# Revit family: Circular diffuser-Extract
name_source: partatom
category: Air Terminals
revit_build: Autodesk Revit MEP 2013 (Build: 20130531_2115(x64)
units: mm (PartAtom-declared; Revit-internal decimal feet)

## types (8) — shared parameters
Manufacturer = Anemostat
Model = C-27
URL = http://www.anemostat.com

## per-type parameters (varying)
| type | A - Outer Cone Radius | A Outer Cone | C1 A | C1 B | C1 B Radius | C1 C | C1 C Radius | C2 & 3 A | C2 B | C2 B Radius | C2 C | C2 C Radius | C3 B | C3 B Radius | C3 C | C3 C Radius | Diffuser Service | Duct | Duct Radius | Outer Cone Height | R Neck Height | U - Outer Cone Radius | U Outer Cone | Z |
| C-27 06" | 276.2 mm | 552.5 mm | 57.9 mm | 102 mm | 51 mm | 34.9 mm | 17.5 mm | 54.8 mm | 217.5 mm | 108.7 mm | 108 mm | 54 mm | 385 mm | 192.5 mm | 209.6 mm | 104.8 mm | SCD | 300 mm | 150 mm | 70.6 mm | 76.2 mm  [stored 0.25 ft] | 308 mm | 616 mm | 25.4 mm  [stored 0.0833333 ft] |
| C-27 08" | 208 mm | 415.9 mm | 42.1 mm | 67.5 mm | 33.7 mm | 27 mm | 13.5 mm | 38.9 mm | 161.9 mm | 81 mm | 84.1 mm | 42.1 mm | 288.1 mm | 144.1 mm | 163.5 mm | 81.8 mm | SCD | 203.2 mm | 101.6 mm | 52.4 mm | 76.2 mm  [stored 0.25 ft] | 233.4 mm | 466.7 mm | 15.9 mm |
| C-27 10" | 276.2 mm | 552.5 mm | 57.9 mm | 102 mm | 51 mm | 34.9 mm | 17.5 mm | 54.8 mm | 217.5 mm | 108.7 mm | 108 mm | 54 mm | 385 mm | 192.5 mm | 209.6 mm | 104.8 mm | SCD | 250 mm | 125 mm | 79.4 mm | 76.2 mm  [stored 0.25 ft] | 308 mm | 616 mm | 25.4 mm  [stored 0.0833333 ft] |
| C-27 12" | 276.2 mm | 552.5 mm | 57.9 mm | 102 mm | 51 mm | 34.9 mm | 17.5 mm | 54.8 mm | 217.5 mm | 108.7 mm | 108 mm | 54 mm | 385 mm | 192.5 mm | 209.6 mm | 104.8 mm | ECD | 300 mm | 150 mm | 70.6 mm | 76.2 mm  [stored 0.25 ft] | 308 mm | 616 mm | 25.4 mm  [stored 0.0833333 ft] |
| C-27 15" | 403.2 mm | 806.5 mm | 76.2 mm  [stored 0.25 ft] | 141.3 mm | 70.6 mm | 38.1 mm  [stored 0.125 ft] | 19.1 mm | 85.7 mm | 311.2 mm | 155.6 mm | 139.7 mm | 69.9 mm | 558.8 mm | 279.4 mm | 284.2 mm | 142.1 mm | SCD | 381 mm | 190.5 mm | 99.2 mm | 76.2 mm  [stored 0.25 ft] | 450.9 mm | 901.7 mm | 34.9 mm |
| C-27 18" | 403.2 mm | 806.5 mm | 76.2 mm  [stored 0.25 ft] | 141.3 mm | 70.6 mm | 38.1 mm  [stored 0.125 ft] | 19.1 mm | 85.7 mm | 311.2 mm | 155.6 mm | 139.7 mm | 69.9 mm | 558.8 mm | 279.4 mm | 284.2 mm | 142.1 mm | SCD | 457.2 mm | 228.6 mm | 76.2 mm  [stored 0.25 ft] | 82.6 mm | 450.9 mm | 901.7 mm | 34.9 mm |
| C-27 21" | 542.9 mm | 1085.9 mm | 96.8 mm | 222.3 mm | 111.1 mm | 71.4 mm | 35.7 mm | 122.6 mm | 473.1 mm | 236.5 mm | 190.5 mm | 95.3 mm | 831.9 mm | 415.9 mm | 355.6 mm | 177.8 mm | SCD | 533.4 mm | 266.7 mm | 173 mm | 114.3 mm | 590.6 mm | 1181.1 mm | 12.7 mm  [stored 0.0416667 ft] |
| C-27 24" | 542.9 mm | 1085.9 mm | 96.8 mm | 222.3 mm | 111.1 mm | 71.4 mm | 35.7 mm | 122.6 mm | 473.1 mm | 236.5 mm | 190.5 mm | 95.3 mm | 831.9 mm | 415.9 mm | 355.6 mm | 177.8 mm | SCD | 609.6 mm | 304.8 mm | 173 mm | 130.2 mm | 590.6 mm | 1181.1 mm | 12.7 mm  [stored 0.0416667 ft] |

note: [stored X ft] marks values corroborated as IEEE doubles in the binary element streams (Revit-internal decimal feet)

## geometry (parser evidence)
native form markers: Sweep x3
no freeform markers — native parametric forms only
